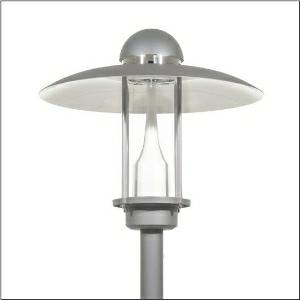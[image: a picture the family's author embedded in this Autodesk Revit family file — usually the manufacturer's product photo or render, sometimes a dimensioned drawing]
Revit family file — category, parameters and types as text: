
# Revit family: city-light_elegance_iq___p1_0a_5xa5265bf14hp_b31b
name_source: partatom
category: Lighting Fixtures
units: mm (PartAtom-declared; Revit-internal decimal feet)

## family parameters
Cut with Voids When Loaded = No
Host = Face
Light Source = No
Part Type = Normal
Room Calculation Point = No
Round Connector Dimension = Use Diameter
Shared = No

## types (1)
- --- (1 x LED, 3710 lm, 33.6 W, 2200K)
    Apparent Load = 34 VA
    CIE Flux Codes = 31 62 91 97 100
    Color Rendering = 70
    Color Temperature = 2200K
    Default Elevation = 1800 mm
    Description = City-Light Elegance iQ, mast luminaire, Module 540 iQ-SR, primary light control with 3 zone facetted reflector, of plastic, silver coated, highly specular, structured, primary optical cover: cover, of PMMA, transparent, light distribution: P1.0a, light emission: direct distribution, primary light characteristic: strongly asymmetric, installation type: post-top, LED, High Power LED, rated luminous flux: 3.710lm, luminous efficacy: 110lm/W, light colour: 722, colour temperature: 2200K, control gear: iQ Street-Remote, control: pre-setting: logarithmic dimming characteristic, Street-Remote, Auto-Match, Temp-Guard, Lumen-Switch, Night-Set, Smart-Wire, Light-Fading, Desk-Remote (wireless, voltage-free reading and setting of iQ features in the workshop via application-optimized NFC function/RFID function), optimised constant luminous flux control (CLO 2.0), with terminal, 6-pole, max. 2.5mm², mains connection: 230..240V, AC, 50/60Hz, start of lifetime: 34W, end of service life: 36W, reduction: 15W, luminaire housing, upper part, of aluminium, coated, Siteco® metallic grey (DB 702S), diameter: 750mm, height: 675mm, spigot size: d x l = 76 x 70mm (post-top) | with reducer (optional accessory) 60 x 70mm, mounting height: 3..5m, post-top mast mounting element, of diecast aluminium, coated, Siteco® metallic grey (DB 702S), Module 540 iQ-SR, traffic white (RAL 9016), equipment: Power, protection rating (complete): IP65, insulation class (complete): insulation class II (safety insulation), certification: CE, ENEC, VDE, packaging unit: 1 piece

Light Distribution: P1.0a
    Height = 675 mm
    Lamp = 1 x LED
    Lamp Light Flux = 3710 lm
    Lamp Power = 33.6 W
    Lamp count = 1
    Length = 750 mm
    Luminous efficacy = 110 lm/W
    Manufacturer = Siteco
    ModVariant = No
    Model = 5XA5265BF14HP
    Number of Poles = 1
    OnlyDefault = Yes
    Power Factor = 1
    Product Name = City-Light Elegance iQ | P1.0a
    Product group = mast luminaire | pylon top
    ProductGroupID = 6100
    Protection Class = Protection class II
    Protection Degree = IP 65
    RLX_Detail_Level = 1
    RLX_Emergency_Light_Flux = 0 lm
    RLX_Emergency_Type = 0
    RLX_Emergency_Type_DB = No
    RlxData = <blob elided: 36861 chars, md5=8a317f4a>
    Socket = socket
    Standby Power = 0 W
    System Light Flux = 3710 lm
    System Power = 34 W
    Type Comments = factory setting: luminous flux: 100 % | dim-lin: 254 | 695 mA
    Type Image = l_1006912.jpg
    URL = http://relux.com
    VarID = @adj_192974
    Voltage = 0 V
    Weight = 0.00 kg
    Width = 0 mm  [stored 0 ft]

note: [stored X ft] marks values corroborated as IEEE doubles in the binary element streams (Revit-internal decimal feet)

## geometry (parser evidence)
native form markers: Blend x4, Sweep x11
no freeform markers — native parametric forms only
